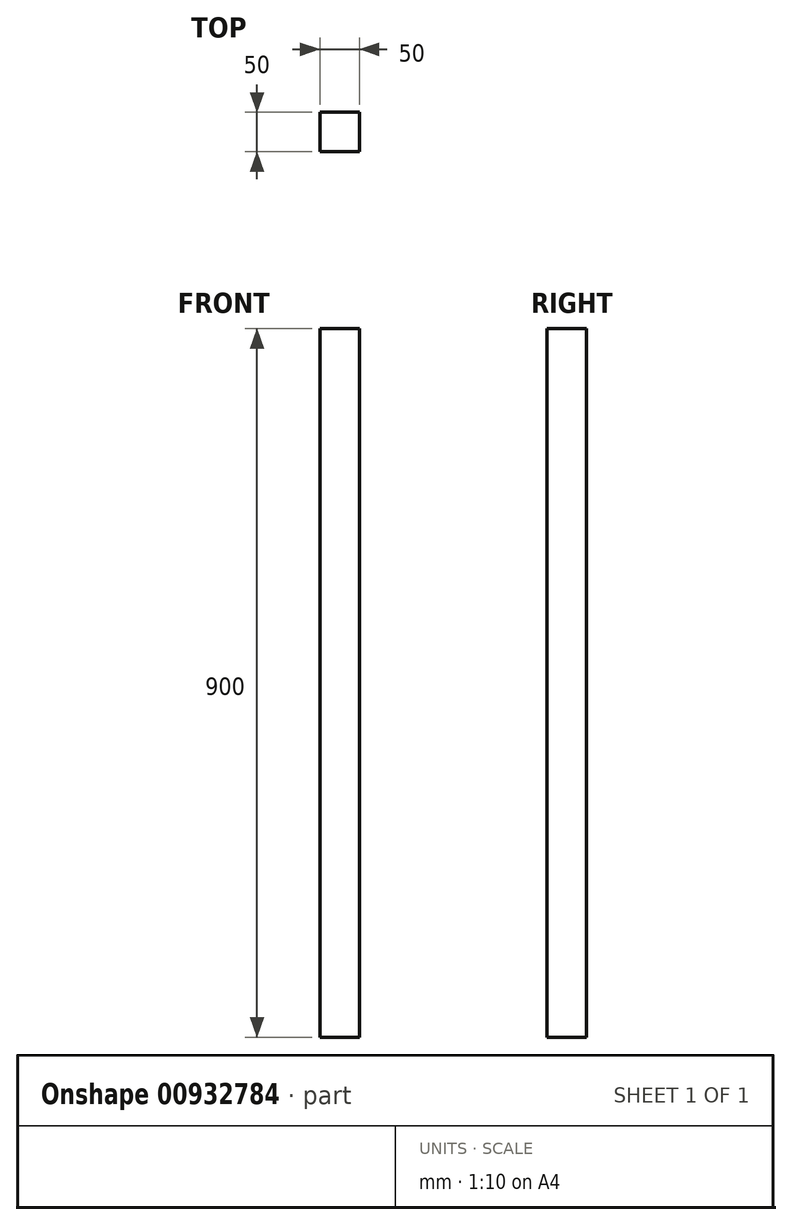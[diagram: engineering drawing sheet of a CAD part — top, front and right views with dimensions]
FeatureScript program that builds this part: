
annotation { "Feature Type Name" : "Feature", "Feature Type Description" : "" }
export const myFeature = defineFeature(function(context is Context, id is Id, definition is map)
    precondition{}
    {
        {
            var Q0;
            Q0=qCreatedBy(makeId("Top.planeOp"),FACE);
            var sketch = newSketch(context, id + "F0", { "sketchPlane" : qUnion([Q0])});
            skLineSegment(sketch, "E0.bottom", {"start": v(-77.8, -40.7) * mm, "end": v(-27.8, -40.7) * mm});
            skLineSegment(sketch, "E0.top", {"start": v(-77.8, -90.7) * mm, "end": v(-27.8, -90.7) * mm});
            skLineSegment(sketch, "E0.left", {"start": v(-77.8, -40.7) * mm, "end": v(-77.8, -90.7) * mm});
            skLineSegment(sketch, "E0.right", {"start": v(-27.8, -40.7) * mm, "end": v(-27.8, -90.7) * mm});
            skSolve(sketch);
        }
        {
            var Q0;
            Q0=makeQuery(id+"F0.imprint","IMPRINT",FACE,{"disambiguationData":[TD([[makeQuery(id+"F0.imprint","IMPRINT",EDGE,{"derivedFrom":sQuery(id+"F0.wireOp",EDGE,"E0.bottom")}),-1.0]])]});
            extrude(context, id + "F1", {"entities" : qUnion([Q0]), "depth" : 900 * mm, "offsetDistance" : 25 * mm});
        }
    });
